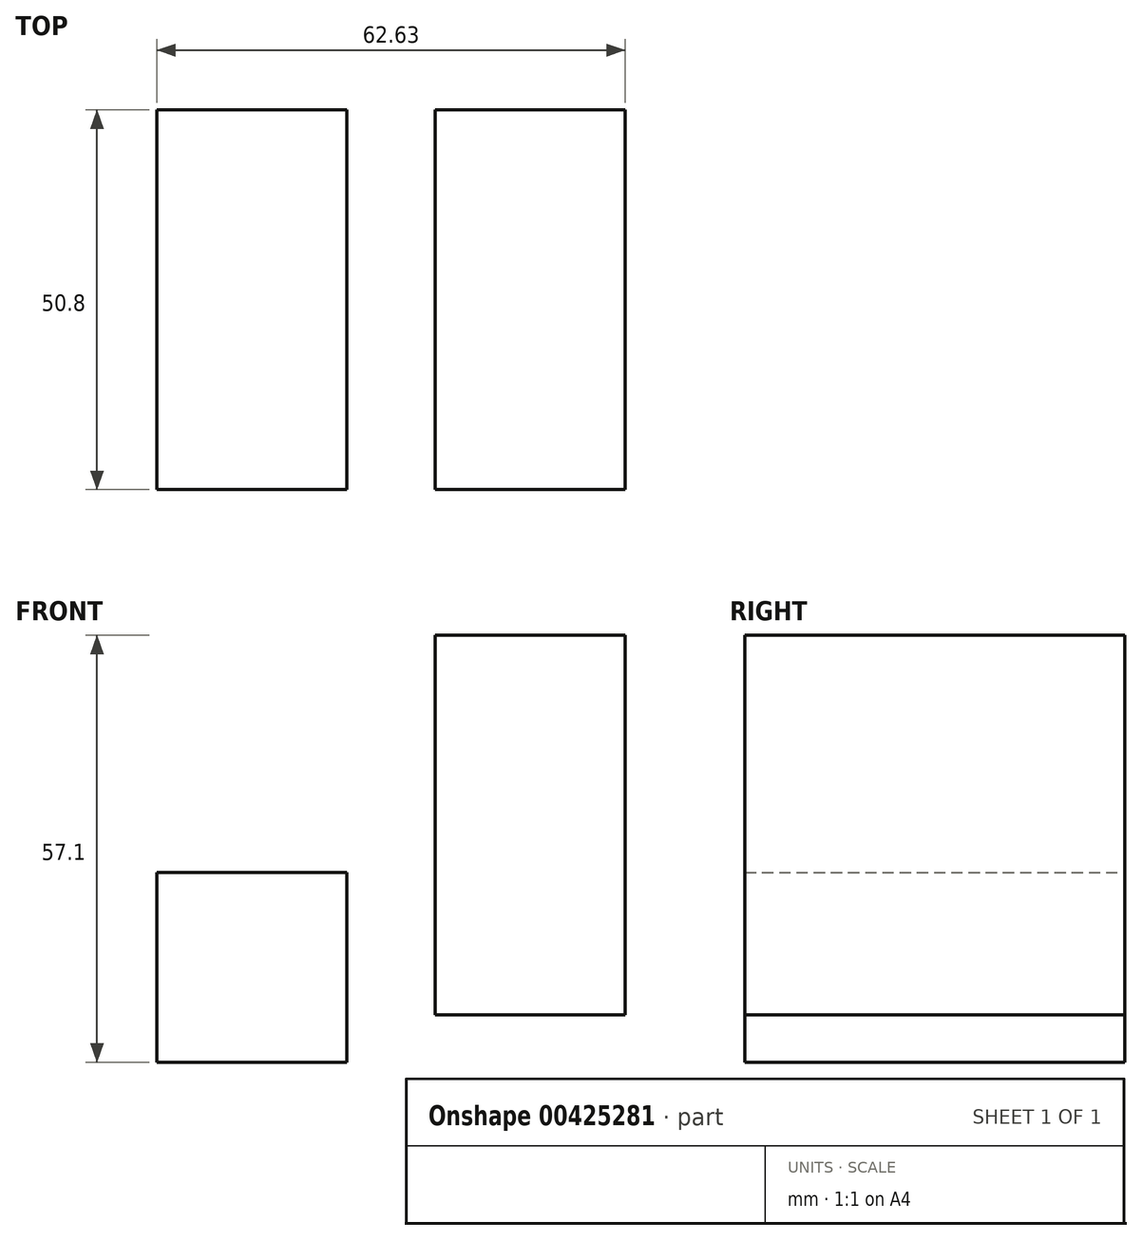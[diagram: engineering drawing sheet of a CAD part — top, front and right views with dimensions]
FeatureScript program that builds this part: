
annotation { "Feature Type Name" : "Feature", "Feature Type Description" : "" }
export const myFeature = defineFeature(function(context is Context, id is Id, definition is map)
    precondition{}
    {
        {
            var Q0;
            Q0=qCreatedBy(makeId("Front.planeOp"),FACE);
            var sketch = newSketch(context, id + "F0", { "sketchPlane" : qUnion([Q0])});
            skLineSegment(sketch, "E0", {"start": v(-44.68, 13.94) * mm, "end": v(-44.68, -11.46) * mm});
            skLineSegment(sketch, "E1", {"start": v(-44.68, -11.46) * mm, "end": v(-19.28, -11.46) * mm});
            skLineSegment(sketch, "E2", {"start": v(-19.28, -11.46) * mm, "end": v(-19.28, 13.94) * mm});
            skLineSegment(sketch, "E3", {"start": v(-44.68, 13.94) * mm, "end": v(-19.28, 13.94) * mm});
            skSolve(sketch);
        }
        {
            var Q0;
            Q0 = qSketchRegion(id + "F0", true);
            extrude(context, id + "F1", {"entities" : qUnion([Q0]), "depth" : 50.8 * mm});
        }
        {
            var Q0;
            Q0=qCreatedBy(makeId("Front.planeOp"),FACE);
            var sketch = newSketch(context, id + "F2", { "sketchPlane" : qUnion([Q0])});
            skLineSegment(sketch, "E4", {"start": v(-7.45, 45.64) * mm, "end": v(-7.45, -5.16) * mm});
            skLineSegment(sketch, "E5", {"start": v(-7.45, 45.64) * mm, "end": v(17.95, 45.64) * mm});
            skLineSegment(sketch, "E6", {"start": v(17.95, 45.64) * mm, "end": v(17.95, -5.16) * mm});
            skLineSegment(sketch, "E7", {"start": v(-7.45, -5.16) * mm, "end": v(17.95, -5.16) * mm});
            skSolve(sketch);
        }
        {
            var Q0;
            Q0 = qSketchRegion(id + "F2", true);
            extrude(context, id + "F3", {"entities" : qUnion([Q0]), "depth" : 50.8 * mm});
        }
    });
